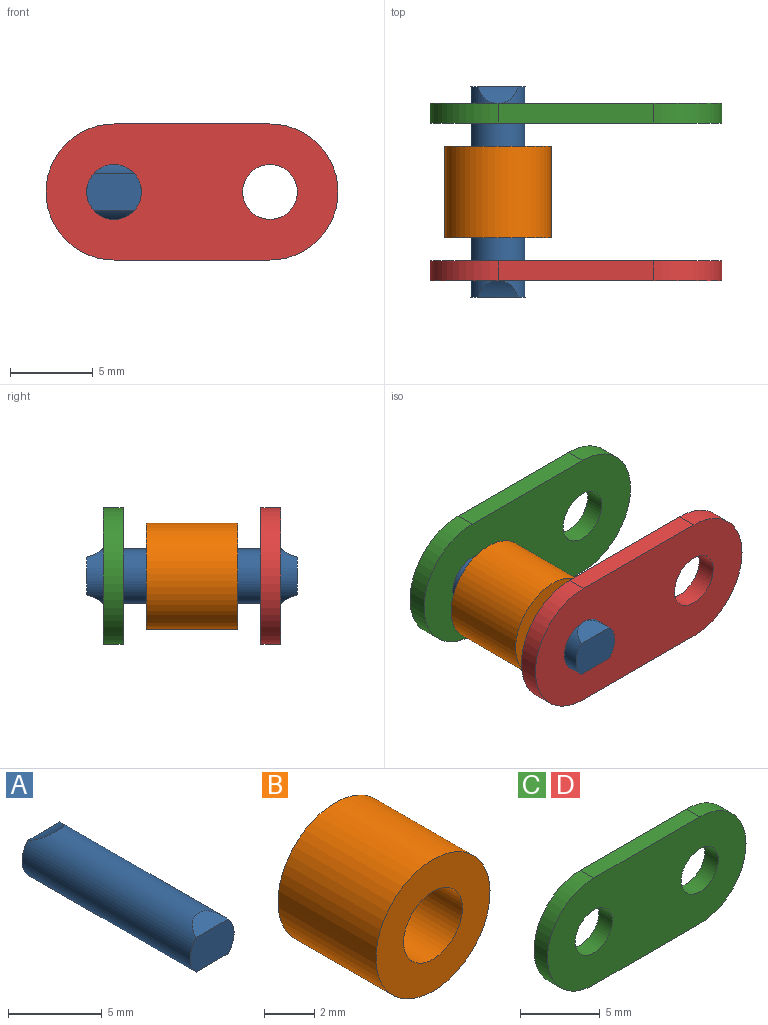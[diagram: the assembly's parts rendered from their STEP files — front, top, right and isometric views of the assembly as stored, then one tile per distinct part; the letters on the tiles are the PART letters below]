
ASSEMBLY  parts=4 mates=3
PART A: 7 faces, bbox 3.3x12.7x3.3 mm
  f0: plane 3.3x2.25mm, normal (0,-1,0), area 6.8mm2, adj f2,f3,f6
  f1: plane 3.3x2.25mm, normal (0,1,0), area 6.8mm2, adj f2,f4,f5
  f2: cylinder r=1.65mm len=12.7mm, axis (0,1,0), area 124mm2, adj f0,f1,f3,f4,f5,f6
  f3: cylinder r=3.3mm len=2.41mm, axis (1,0,0), area 2mm2, adj f0,f2
  f4: cylinder r=3.3mm len=2.41mm, axis (1,0,0), area 2mm2, adj f1,f2
  f5: cylinder r=3.3mm len=2.41mm, axis (1,0,0), area 2mm2, adj f1,f2
  f6: cylinder r=3.3mm len=2.41mm, axis (1,0,0), area 2mm2, adj f0,f2
PART B: 4 faces, bbox 6.4x5.5x6.4 mm
  f0: cylinder r=1.65mm len=5.5mm, axis (0,1,0), area 57mm2, adj f2,f3
  f1: cylinder r=3.2mm len=6.4mm, axis (0,1,0), area 110.6mm2, adj f2,f3
  f2: plane 6.4x6.4mm, normal (0,-1,0), area 23.6mm2, adj f0,f1
  f3: plane 6.4x6.4mm, normal (0,1,0), area 23.6mm2, adj f0,f1
PART C: 8 faces, bbox 17.6x1.2x8.2 mm
  f0: plane 9.4x1.2mm, normal (0,0,1), area 11.3mm2, adj f1,f5,f6,f7
  f1: cylinder r=4.1mm len=8.2mm, axis (0,1,0), area 15.5mm2, adj f0,f2,f6,f7
  f2: plane 9.4x1.2mm, normal (0,0,-1), area 11.3mm2, adj f1,f5,f6,f7
  f3: cylinder r=1.65mm len=3.3mm, axis (0,1,0), area 12.4mm2, adj f6,f7
  f4: cylinder r=1.65mm len=3.3mm, axis (0,1,0), area 12.4mm2, adj f6,f7
  f5: cylinder r=4.1mm len=8.2mm, axis (0,1,0), area 15.5mm2, adj f0,f2,f6,f7
  f6: plane 17.6x8.2mm, normal (0,-1,0), area 112.8mm2, adj f0,f1,f2,f3,f4,f5
  f7: plane 17.6x8.2mm, normal (0,1,0), area 112.8mm2, adj f0,f1,f2,f3,f4,f5
PART D: same geometry as C
PLACE A t=(0,-6.35,0)mm
PLACE B t=(0,2.75,0)mm
PLACE C t=(0,5.35,0)mm
PLACE D t=(0,-4.15,0)mm
MATE fastened B.f1 <-> A.f2  axis (0,1,0) through (0,0,0)mm
MATE fastened C.f1 <-> B.f1  axis (0,-1,0) through (0,4.15,0)mm
MATE fastened D.f3 <-> B.f1  axis (0,1,0) through (0,-4.15,0)mm
